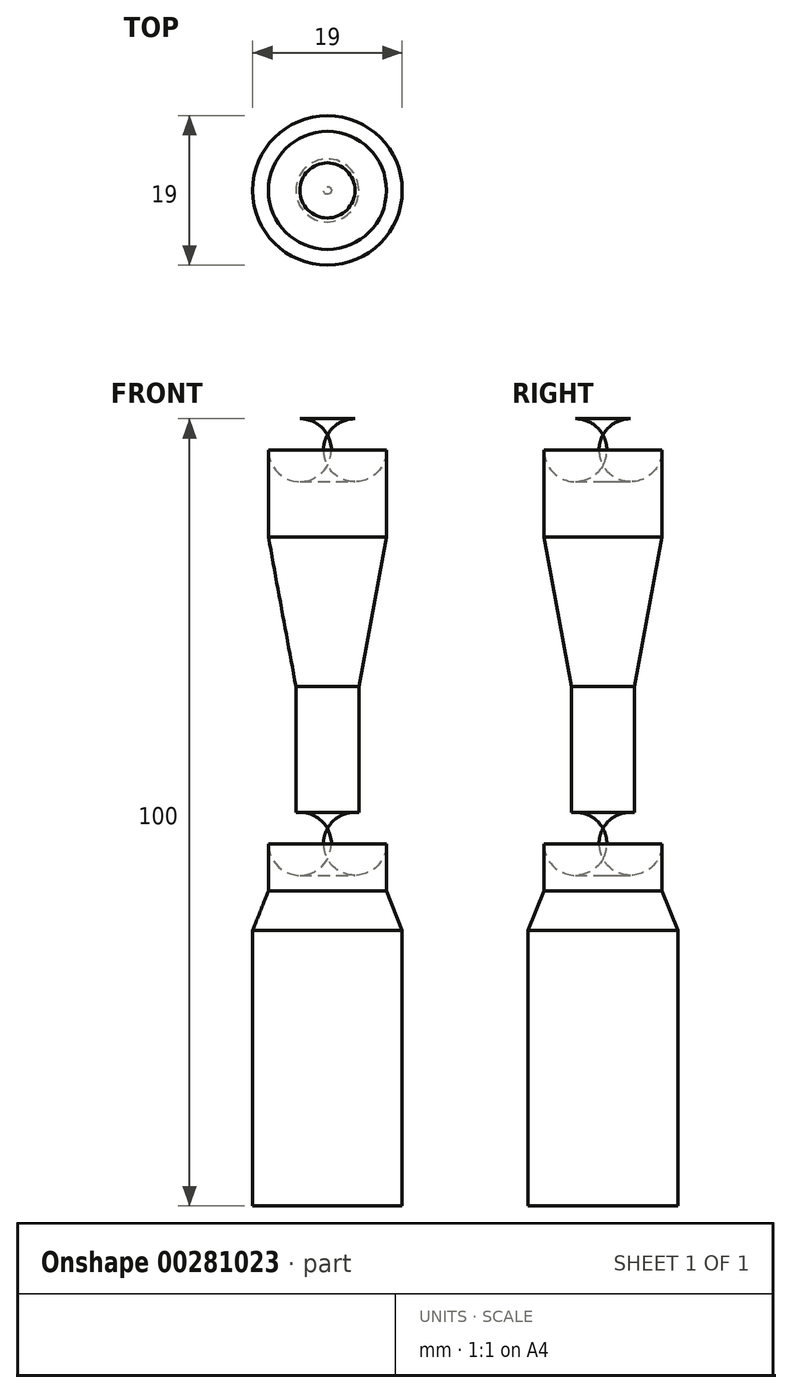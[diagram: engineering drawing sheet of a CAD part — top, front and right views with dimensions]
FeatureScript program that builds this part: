
annotation { "Feature Type Name" : "Feature", "Feature Type Description" : "" }
export const myFeature = defineFeature(function(context is Context, id is Id, definition is map)
    precondition{}
    {
        {
            var Q0;
            Q0=qCreatedBy(makeId("Front.planeOp"),FACE);
            var sketch = newSketch(context, id + "F0", { "sketchPlane" : qUnion([Q0])});
            skLineSegment(sketch, "E0", {"start": v(0, 0) * mm, "end": v(3.5, 0) * mm});
            skLineSegment(sketch, "E1", {"start": v(7.5, -4) * mm, "end": v(7.5, -15) * mm});
            skLineSegment(sketch, "E2", {"start": v(7.5, -15) * mm, "end": v(4, -34) * mm});
            skLineSegment(sketch, "E3", {"start": v(4, -34) * mm, "end": v(4, -50) * mm});
            skLineSegment(sketch, "E4", {"start": v(3.5, -50) * mm, "end": v(4, -50) * mm});
            skLineSegment(sketch, "E5", {"start": v(7.5, -54) * mm, "end": v(7.5, -60) * mm});
            skLineSegment(sketch, "E6", {"start": v(7.5, -60) * mm, "end": v(9.5, -65) * mm});
            skLineSegment(sketch, "E7", {"start": v(9.5, -65) * mm, "end": v(9.5, -100) * mm});
            skLineSegment(sketch, "E8", {"start": v(9.5, -100) * mm, "end": v(0, -100) * mm});
            skLineSegment(sketch, "E9", {"start": v(0, -100) * mm, "end": v(0, 0) * mm});
            skPoint(sketch, "E10.visualSharp", {"position": v(7.5, 0) * mm});
            skArc(sketch, "E10.filletArc", {"start": v(7.5, -4) * mm, "mid": v(6.33, -1.17) * mm, "end": v(3.5, 0) * mm});
            skPoint(sketch, "E11.visualSharp", {"position": v(7.5, -50) * mm});
            skArc(sketch, "E11.filletArc", {"start": v(7.5, -54) * mm, "mid": v(6.33, -51.17) * mm, "end": v(3.5, -50) * mm});
            skSolve(sketch);
        }
        {
            var Q0;
            Q0=makeQuery(id+"F0.imprint","IMPRINT",FACE,{"disambiguationData":[TD([[makeQuery(id+"F0.imprint","IMPRINT",EDGE,{"derivedFrom":sQuery(id+"F0.wireOp",EDGE,"E0")}),-1.0]])]});
            var Q1;
            Q1=sQuery(id+"F0.wireOp",EDGE,"E9");
            revolve(context, id + "F1", {"entities" : qUnion([Q0]), "axis" : qUnion([Q1]), "revolveType" : RevolveType.FULL});
        }
    });
